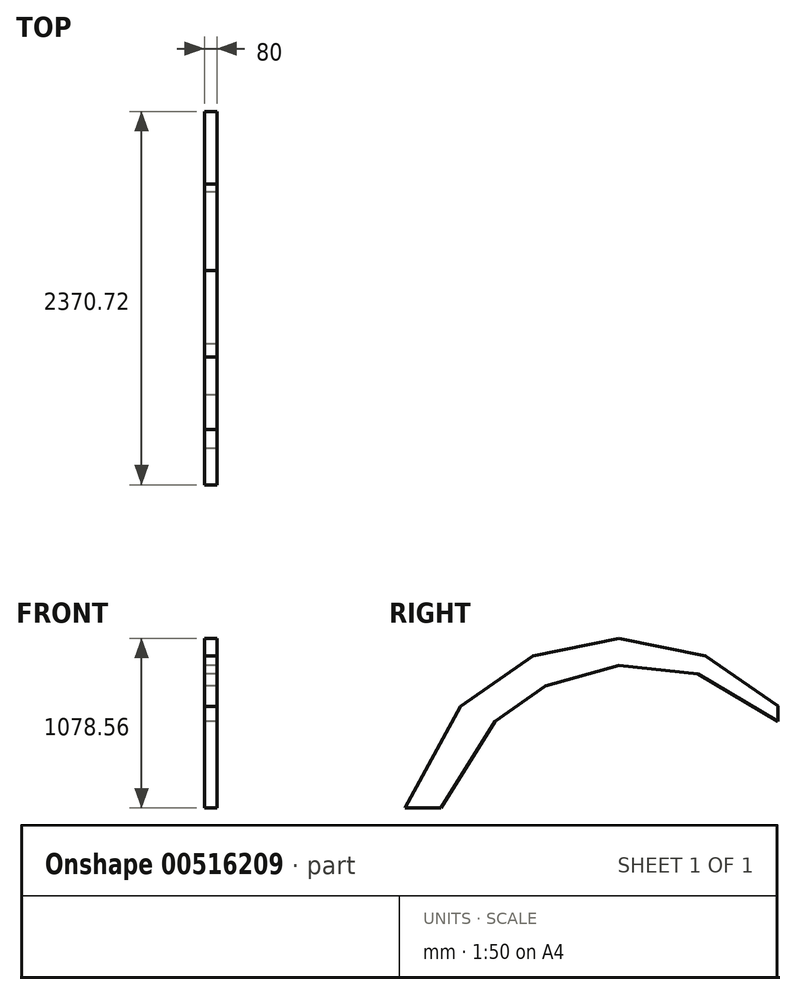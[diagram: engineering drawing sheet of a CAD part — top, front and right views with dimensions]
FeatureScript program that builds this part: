
annotation { "Feature Type Name" : "Feature", "Feature Type Description" : "" }
export const myFeature = defineFeature(function(context is Context, id is Id, definition is map)
    precondition{}
    {
        {
            var Q0;
            Q0=qCreatedBy(makeId("Right.planeOp"),FACE);
            var sketch = newSketch(context, id + "F0", { "sketchPlane" : qUnion([Q0])});
            skLineSegment(sketch, "E0", {"start": v(0, 0) * mm, "end": v(351.56, 646.96) * mm});
            skLineSegment(sketch, "E1", {"start": v(351.56, 646.96) * mm, "end": v(811.98, 965.74) * mm});
            skLineSegment(sketch, "E2", {"start": v(2370.72, 650) * mm, "end": v(1909.35, 967.39) * mm});
            skLineSegment(sketch, "E3", {"start": v(2370.72, 650) * mm, "end": v(2370.72, 550) * mm});
            skLineSegment(sketch, "E4", {"start": v(570.72, 550) * mm, "end": v(230, 0) * mm});
            skLineSegment(sketch, "E5", {"start": v(230, 0) * mm, "end": v(0, 0) * mm});
            skLineSegment(sketch, "E6", {"start": v(811.98, 965.74) * mm, "end": v(1360.5, 1078.56) * mm});
            skLineSegment(sketch, "E7", {"start": v(1360.5, 1078.56) * mm, "end": v(1909.35, 967.39) * mm});
            skLineSegment(sketch, "E8", {"start": v(115, 0) * mm, "end": v(450, 580.24) * mm});
            skLineSegment(sketch, "E9", {"start": v(570.72, 550) * mm, "end": v(892.94, 776.47) * mm});
            skLineSegment(sketch, "E10", {"start": v(892.94, 776.47) * mm, "end": v(1360.5, 907.24) * mm});
            skLineSegment(sketch, "E11", {"start": v(1360.5, 907.24) * mm, "end": v(1860.45, 852.12) * mm});
            skLineSegment(sketch, "E12", {"start": v(1860.45, 852.12) * mm, "end": v(2370.72, 550) * mm});
            skArc(sketch, "E13", {"start": v(2370.72, 650) * mm, "mid": v(992.41, 1028.73) * mm, "end": v(0, 0) * mm, "construction": true});
            skArc(sketch, "E14", {"start": v(2370.72, 550) * mm, "mid": v(1147.23, 871.02) * mm, "end": v(230, 0) * mm, "construction": true});
            skLineSegment(sketch, "E15", {"start": v(811.98, 965.74) * mm, "end": v(958.16, 624) * mm, "construction": true});
            skLineSegment(sketch, "E16", {"start": v(1909.35, 967.39) * mm, "end": v(1764.2, 625.21) * mm, "construction": true});
            skSolve(sketch);
        }
        {
            var Q0;
            Q0 = qSketchRegion(id + "F0", true);
            extrude(context, id + "F1", {"entities" : qUnion([Q0]), "depth" : 80 * mm, "offsetDistance" : 25 * mm});
        }
    });
